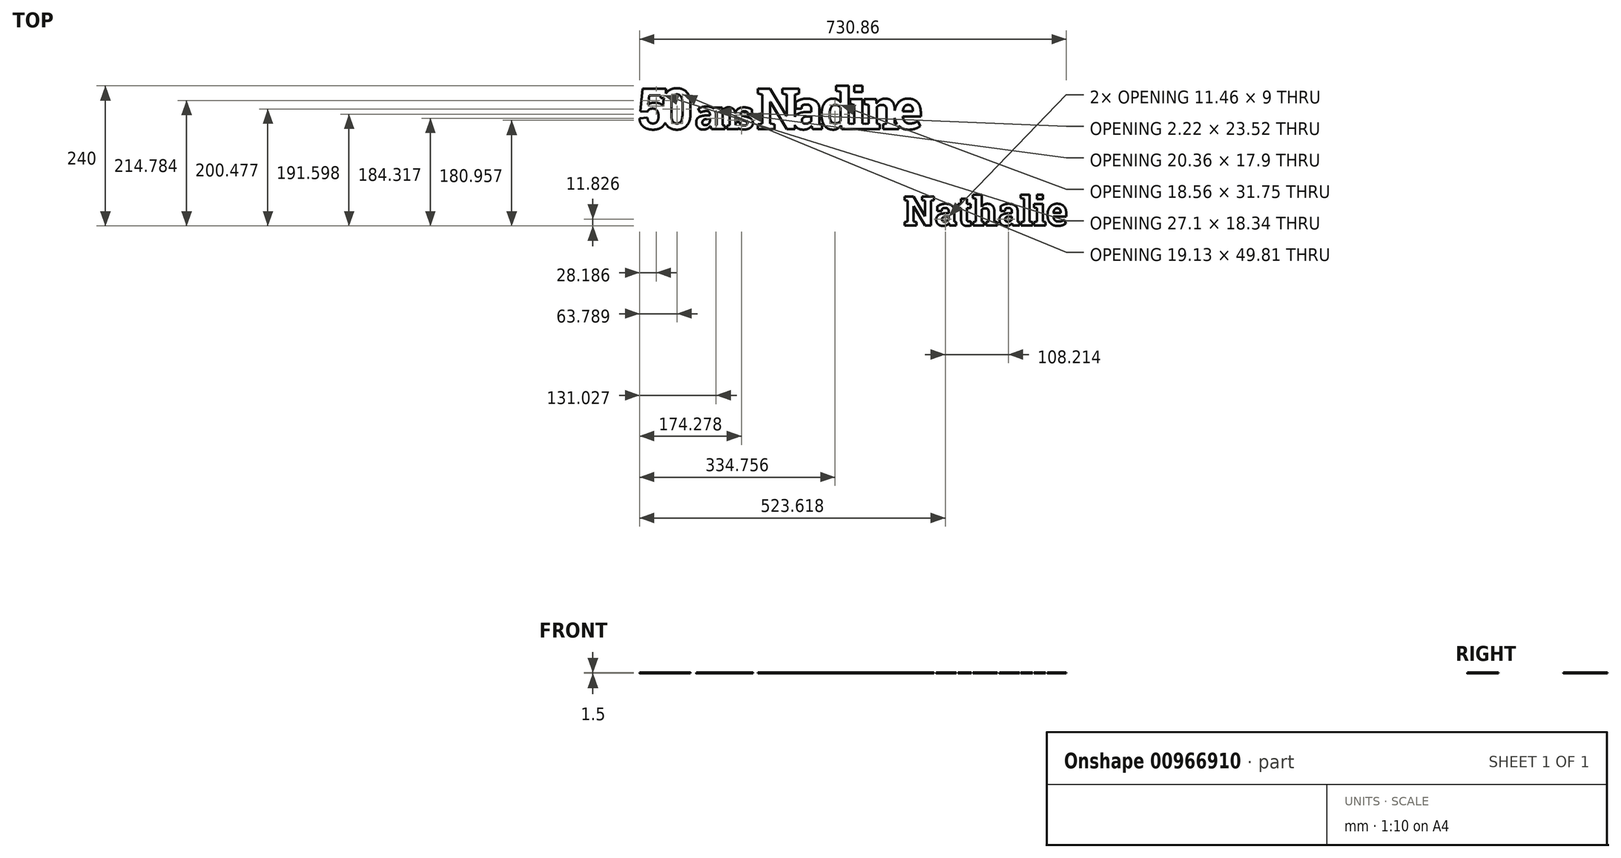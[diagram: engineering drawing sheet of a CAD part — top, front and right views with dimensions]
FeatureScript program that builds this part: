
annotation { "Feature Type Name" : "Feature", "Feature Type Description" : "" }
export const myFeature = defineFeature(function(context is Context, id is Id, definition is map)
    precondition{}
    {
        {
            var Q0;
            Q0=qCreatedBy(makeId("Top.planeOp"),FACE);
            var sketch = newSketch(context, id + "F0", { "sketchPlane" : qUnion([Q0])});
            skText(sketch, "E0", { "text": "50 ans Nathalie", "fontName": "RobotoSlab-Bold.ttf"});
            skText(sketch, "E1", { "text": "5", "fontName": "RobotoSlab-Bold.ttf"});
            skText(sketch, "E2", { "text": "0", "fontName": "RobotoSlab-Bold.ttf"});
            skLineSegment(sketch, "E3", {"start": v(-280.2, 70) * mm, "end": v(280.2, 70) * mm, "construction": true});
            skLineSegment(sketch, "E4", {"start": v(-280.2, 0) * mm, "end": v(280.2, 0) * mm, "construction": true});
            skText(sketch, "E5", { "text": "a", "fontName": "OpenSans-Bold.ttf"});
            skText(sketch, "E6", { "text": "n", "fontName": "RobotoSlab-Bold.ttf"});
            skText(sketch, "E7", { "text": "s", "fontName": "RobotoSlab-Bold.ttf"});
            skLineSegment(sketch, "E8", {"start": v(-280.2, 50) * mm, "end": v(280.2, 50) * mm, "construction": true});
            skText(sketch, "E9", { "text": "N", "fontName": "RobotoSlab-Bold.ttf"});
            skText(sketch, "E10", { "text": "a", "fontName": "RobotoSlab-Bold.ttf"});
            skLineSegment(sketch, "E11", {"start": v(280.2, 70) * mm, "end": v(280.2, 0) * mm, "construction": true});
            skText(sketch, "E12", { "text": "i", "fontName": "RobotoSlab-Bold.ttf"});
            skText(sketch, "E13", { "text": "e", "fontName": "RobotoSlab-Bold.ttf"});
            skText(sketch, "E14", { "text": "d", "fontName": "RobotoSlab-Bold.ttf"});
            skText(sketch, "E15", { "text": "n", "fontName": "RobotoSlab-Bold.ttf"});
            const initialGuessF0  = {"E0": [-0.0539, -0.16522, 1, 0, 0.05], "E1": [-0.2802, 0, 1, 0, 0.07], "E2": [-0.24123, 0, 1, 0, 0.07], "E5": [-0.18318, 0, 1, 0, 0.05], "E6": [-0.15123, 0, 1, 0, 0.05], "E7": [-0.11641, 0, 1, 0, 0.05], "E9": [-0.0772, 0, 1, 0, 0.07], "E10": [-0.0164, 0, 1, 0, 0.07], "E12": [0.08157, 0, 1, 0, 0.07], "E13": [0.15634, 0, 1, 0, 0.07], "E14": [0.0314, 0, 1, 0, 0.07], "E15": [0.1063, 0, 1, 0, 0.07]};
            skSetInitialGuess(sketch, initialGuessF0);
            skSolve(sketch);
        }
        {
            var Q0;
            {var subQ4=sQuery(id+"F0.wireOp",EDGE,"E13.sketch_text.stroke-1");var subQ9=sQuery(id+"F0.wireOp",EDGE,"E13.sketch_text.stroke-0");var subQ10=makeQuery(id+"F0.imprint","INTERSECT",VERTEX,{"derivedFrom":[subQ9,subQ4]});var subQ15=makeQuery(id+"F0.imprint","IMPRINT",EDGE,{"disambiguationData":[TD([[subQ10,1.0]])],"derivedFrom":subQ9});var subQ16=sQuery(id+"F0.wireOp",EDGE,"E12.sketch_text.stroke-7");var subQ21=sQuery(id+"F0.wireOp",EDGE,"E13.sketch_text.stroke-2");var subQ23=makeQuery(id+"F0.imprint","IMPRINT",EDGE,{"derivedFrom":subQ21});var subQ24=makeQuery(id+"F0.imprint","IMPRINT",EDGE,{"derivedFrom":subQ16});var subQ33=sQuery(id+"F0.wireOp",EDGE,"E12.sketch_text.stroke-9");var subQ34=makeQuery(id+"F0.imprint","IMPRINT",EDGE,{"derivedFrom":subQ33});var subQ43=sQuery(id+"F0.wireOp",EDGE,"E12.sketch_text.stroke-1");var subQ48=sQuery(id+"F0.wireOp",EDGE,"E13.sketch_text.stroke-4");var subQ57=sQuery(id+"F0.wireOp",EDGE,"E6.sketch_text.stroke-11");var subQ59=sQuery(id+"F0.wireOp",EDGE,"E7.sketch_text.stroke-14");var subQ60=makeQuery(id+"F0.imprint","INTERSECT",VERTEX,{"derivedFrom":[subQ57,subQ59]});var subQ61=sQuery(id+"F0.wireOp",EDGE,"E6.sketch_text.stroke-9");var subQ64=sQuery(id+"F0.wireOp",EDGE,"E7.sketch_text.stroke-25");var subQ66=makeQuery(id+"F0.imprint","INTERSECT",VERTEX,{"derivedFrom":[subQ61,subQ64]});var subQ69=sQuery(id+"F0.wireOp",EDGE,"E6.sketch_text.stroke-1");var subQ79=sQuery(id+"F0.wireOp",EDGE,"E6.sketch_text.stroke-2");var subQ80=sQuery(id+"F0.wireOp",EDGE,"E5.sketch_text.stroke-15");var subQ81=makeQuery(id+"F0.imprint","INTERSECT",VERTEX,{"derivedFrom":[subQ80,subQ79]});var subQ85=makeQuery(id+"F0.imprint","IMPRINT",EDGE,{"disambiguationData":[TD([[subQ81,1.0]])],"derivedFrom":subQ80});var subQ88=sQuery(id+"F0.wireOp",EDGE,"E5.sketch_text.stroke-0");var subQ89=sQuery(id+"F0.wireOp",EDGE,"E6.sketch_text.stroke-25");var subQ93=makeQuery(id+"F0.imprint","IMPRINT",EDGE,{"derivedFrom":subQ89});var subQ102=makeQuery(id+"F0.imprint","IMPRINT",EDGE,{"disambiguationData":[TD([[subQ66,-1.0]])],"derivedFrom":subQ61});var subQ103=makeQuery(id+"F0.imprint","IMPRINT",EDGE,{"disambiguationData":[TD([[subQ60,-1.0]])],"derivedFrom":subQ57});var subQ108=sQuery(id+"F0.wireOp",EDGE,"E1.sketch_text.stroke-24");var subQ110=sQuery(id+"F0.wireOp",EDGE,"E1.sketch_text.stroke-25");var subQ114=makeQuery(id+"F0.imprint","INTERSECT",VERTEX,{"derivedFrom":[subQ108,subQ110]});var subQ115=makeQuery(id+"F0.imprint","IMPRINT",EDGE,{"disambiguationData":[TD([[subQ114,1.0]])],"derivedFrom":subQ108});var subQ116=sQuery(id+"F0.wireOp",EDGE,"E1.sketch_text.stroke-6");var subQ117=makeQuery(id+"F0.imprint","IMPRINT",EDGE,{"derivedFrom":subQ116});var subQ127=sQuery(id+"F0.wireOp",EDGE,"E1.sketch_text.stroke-0");var subQ135=sQuery(id+"F0.wireOp",EDGE,"E10.sketch_text.stroke-6");var subQ136=sQuery(id+"F0.wireOp",EDGE,"E9.sketch_text.stroke-2");var subQ137=makeQuery(id+"F0.imprint","INTERSECT",VERTEX,{"derivedFrom":[subQ136,subQ135]});var subQ140=makeQuery(id+"F0.imprint","IMPRINT",EDGE,{"disambiguationData":[TD([[subQ137,-1.0]])],"derivedFrom":subQ136});Q0=qUnion([makeQuery(id+"F0.imprint","IMPRINT",FACE,{"disambiguationData":[TD([[makeQuery(id+"F0.imprint","IMPRINT",EDGE,{"derivedFrom":sQuery(id+"F0.wireOp",EDGE,"E0.sketch_text.stroke-0")}),-1.0]])]}),makeQuery(id+"F0.imprint","IMPRINT",FACE,{"disambiguationData":[TD([[makeQuery(id+"F0.imprint","IMPRINT",EDGE,{"derivedFrom":sQuery(id+"F0.wireOp",EDGE,"E0.sketch_text.stroke-81")}),-1.0]])]}),makeQuery(id+"F0.imprint","IMPRINT",FACE,{"disambiguationData":[TD([[makeQuery(id+"F0.imprint","IMPRINT",EDGE,{"derivedFrom":sQuery(id+"F0.wireOp",EDGE,"E0.sketch_text.stroke-107")}),-1.0]])]}),makeQuery(id+"F0.imprint","IMPRINT",FACE,{"disambiguationData":[TD([[makeQuery(id+"F0.imprint","IMPRINT",EDGE,{"derivedFrom":sQuery(id+"F0.wireOp",EDGE,"E0.sketch_text.stroke-137")}),-1.0]])]}),makeQuery(id+"F0.imprint","IMPRINT",FACE,{"disambiguationData":[TD([[makeQuery(id+"F0.imprint","IMPRINT",EDGE,{"derivedFrom":sQuery(id+"F0.wireOp",EDGE,"E0.sketch_text.stroke-196")}),-1.0]])]}),makeQuery(id+"F0.imprint","IMPRINT",FACE,{"disambiguationData":[TD([[makeQuery(id+"F0.imprint","IMPRINT",EDGE,{"derivedFrom":sQuery(id+"F0.wireOp",EDGE,"E0.sketch_text.stroke-216")}),-1.0]])]}),makeQuery(id+"F0.imprint","IMPRINT",FACE,{"disambiguationData":[TD([[makeQuery(id+"F0.imprint","IMPRINT",EDGE,{"derivedFrom":sQuery(id+"F0.wireOp",EDGE,"E0.sketch_text.stroke-277")}),-1.0]])]}),makeQuery(id+"F0.imprint","IMPRINT",FACE,{"disambiguationData":[TD([[makeQuery(id+"F0.imprint","IMPRINT",EDGE,{"derivedFrom":sQuery(id+"F0.wireOp",EDGE,"E0.sketch_text.stroke-287")}),-1.0]])]}),makeQuery(id+"F0.imprint","IMPRINT",FACE,{"disambiguationData":[TD([[makeQuery(id+"F0.imprint","IMPRINT",EDGE,{"derivedFrom":sQuery(id+"F0.wireOp",EDGE,"E0.sketch_text.stroke-297")}),-1.0]])]}),makeQuery(id+"F0.imprint","IMPRINT",FACE,{"disambiguationData":[TD([[makeQuery(id+"F0.imprint","IMPRINT",EDGE,{"derivedFrom":sQuery(id+"F0.wireOp",EDGE,"E12.sketch_text.stroke-10")}),-1.0]])]}),makeQuery(id+"F0.imprint","IMPRINT",FACE,{"disambiguationData":[TD([[makeQuery(id+"F0.imprint","IMPRINT",EDGE,{"derivedFrom":sQuery(id+"F0.wireOp",EDGE,"E0.sketch_text.stroke-26")}),-1.0]])]}),makeQuery(id+"F0.imprint","IMPRINT",FACE,{"disambiguationData":[TD([[makeQuery(id+"F0.imprint","IMPRINT",EDGE,{"derivedFrom":sQuery(id+"F0.wireOp",EDGE,"E0.sketch_text.stroke-46")}),-1.0]])]}),makeQuery(id+"F0.imprint","IMPRINT",FACE,{"disambiguationData":[TD([[makeQuery(id+"F0.imprint","IMPRINT",EDGE,{"derivedFrom":sQuery(id+"F0.wireOp",EDGE,"E0.sketch_text.stroke-161")}),-1.0]])]}),makeQuery(id+"F0.imprint","IMPRINT",FACE,{"disambiguationData":[TD([[makeQuery(id+"F0.imprint","IMPRINT",EDGE,{"derivedFrom":sQuery(id+"F0.wireOp",EDGE,"E0.sketch_text.stroke-242")}),-1.0]])]}),makeQuery(id+"F0.imprint","IMPRINT",FACE,{"disambiguationData":[TD([[makeQuery(id+"F0.imprint","IMPRINT",EDGE,{"derivedFrom":sQuery(id+"F0.wireOp",EDGE,"E0.sketch_text.stroke-301")}),-1.0]])]}),makeQuery(id+"F0.imprint","IMPRINT",FACE,{"disambiguationData":[TD([[makeQuery(id+"F0.imprint","IMPRINT",EDGE,{"derivedFrom":sQuery(id+"F0.wireOp",EDGE,"E9.sketch_text.stroke-0")}),-1.0]])]}),makeQuery(id+"F0.imprint","IMPRINT",FACE,{"disambiguationData":[TD([[makeQuery(id+"F0.imprint","IMPRINT",EDGE,{"derivedFrom":sQuery(id+"F0.wireOp",EDGE,"E10.sketch_text.stroke-0")}),-1.0]])]}),makeQuery(id+"F0.imprint","IMPRINT",FACE,{"disambiguationData":[TD([[subQ140,-1.0]])]}),makeQuery(id+"F0.imprint","IMPRINT",FACE,{"disambiguationData":[TD([[subQ117,-1.0]])]}),makeQuery(id+"F0.imprint","IMPRINT",FACE,{"disambiguationData":[TD([[subQ115,-1.0]])]}),makeQuery(id+"F0.imprint","IMPRINT",FACE,{"disambiguationData":[TD([[makeQuery(id+"F0.imprint","IMPRINT",EDGE,{"derivedFrom":subQ127}),-1.0]])]}),makeQuery(id+"F0.imprint","IMPRINT",FACE,{"disambiguationData":[TD([[subQ117,1.0]])]}),makeQuery(id+"F0.imprint","IMPRINT",FACE,{"disambiguationData":[TD([[subQ85,-1.0]])]}),makeQuery(id+"F0.imprint","IMPRINT",FACE,{"disambiguationData":[TD([[subQ93,-1.0]])]}),makeQuery(id+"F0.imprint","IMPRINT",FACE,{"disambiguationData":[TD([[subQ102,-1.0]])]}),makeQuery(id+"F0.imprint","IMPRINT",FACE,{"disambiguationData":[TD([[subQ103,-1.0]])]}),makeQuery(id+"F0.imprint","IMPRINT",FACE,{"disambiguationData":[TD([[makeQuery(id+"F0.imprint","IMPRINT",EDGE,{"derivedFrom":sQuery(id+"F0.wireOp",EDGE,"E7.sketch_text.stroke-0")}),-1.0]])]}),makeQuery(id+"F0.imprint","IMPRINT",FACE,{"disambiguationData":[TD([[makeQuery(id+"F0.imprint","IMPRINT",EDGE,{"derivedFrom":subQ88}),-1.0]])]}),makeQuery(id+"F0.imprint","IMPRINT",FACE,{"disambiguationData":[TD([[makeQuery(id+"F0.imprint","IMPRINT",EDGE,{"derivedFrom":subQ69}),-1.0]])]}),makeQuery(id+"F0.imprint","IMPRINT",FACE,{"disambiguationData":[TD([[subQ15,-1.0]])]}),makeQuery(id+"F0.imprint","IMPRINT",FACE,{"disambiguationData":[TD([[subQ24,-1.0]])]}),makeQuery(id+"F0.imprint","IMPRINT",FACE,{"disambiguationData":[TD([[subQ34,1.0]])]}),makeQuery(id+"F0.imprint","IMPRINT",FACE,{"disambiguationData":[TD([[subQ23,-1.0]])]}),makeQuery(id+"F0.imprint","IMPRINT",FACE,{"disambiguationData":[TD([[makeQuery(id+"F0.imprint","IMPRINT",EDGE,{"derivedFrom":subQ48}),-1.0]])]}),makeQuery(id+"F0.imprint","IMPRINT",FACE,{"disambiguationData":[TD([[makeQuery(id+"F0.imprint","IMPRINT",EDGE,{"derivedFrom":subQ43}),-1.0]])]}),makeQuery(id+"F0.imprint","IMPRINT",FACE,{"disambiguationData":[TD([[subQ34,-1.0]])]}),makeQuery(id+"F0.imprint","IMPRINT",FACE,{"disambiguationData":[TD([[subQ24,1.0]])]})]);}
            extrude(context, id + "F1", {"entities" : qUnion([Q0]), "depth" : 1.5 * mm, "offsetDistance" : 25 * mm});
        }
        {
            var Q0;
            Q0=makeQuery(id+"F1.opExtrude","SWEPT_BODY",BODY,{"disambiguationData":[OSD([sQuery(id+"F0.wireOp",EDGE,"E0.sketch_text.stroke-0"),sQuery(id+"F0.wireOp",EDGE,"E0.sketch_text.stroke-1"),sQuery(id+"F0.wireOp",EDGE,"E0.sketch_text.stroke-2"),sQuery(id+"F0.wireOp",EDGE,"E0.sketch_text.stroke-3"),sQuery(id+"F0.wireOp",EDGE,"E0.sketch_text.stroke-4"),sQuery(id+"F0.wireOp",EDGE,"E0.sketch_text.stroke-5"),sQuery(id+"F0.wireOp",EDGE,"E0.sketch_text.stroke-6"),sQuery(id+"F0.wireOp",EDGE,"E0.sketch_text.stroke-7"),sQuery(id+"F0.wireOp",EDGE,"E0.sketch_text.stroke-8"),sQuery(id+"F0.wireOp",EDGE,"E0.sketch_text.stroke-9"),sQuery(id+"F0.wireOp",EDGE,"E0.sketch_text.stroke-10"),sQuery(id+"F0.wireOp",EDGE,"E0.sketch_text.stroke-11"),sQuery(id+"F0.wireOp",EDGE,"E0.sketch_text.stroke-12"),sQuery(id+"F0.wireOp",EDGE,"E0.sketch_text.stroke-13"),sQuery(id+"F0.wireOp",EDGE,"E0.sketch_text.stroke-14"),sQuery(id+"F0.wireOp",EDGE,"E0.sketch_text.stroke-15"),sQuery(id+"F0.wireOp",EDGE,"E0.sketch_text.stroke-16"),sQuery(id+"F0.wireOp",EDGE,"E0.sketch_text.stroke-17"),sQuery(id+"F0.wireOp",EDGE,"E0.sketch_text.stroke-18"),sQuery(id+"F0.wireOp",EDGE,"E0.sketch_text.stroke-19"),sQuery(id+"F0.wireOp",EDGE,"E0.sketch_text.stroke-20"),sQuery(id+"F0.wireOp",EDGE,"E0.sketch_text.stroke-21"),sQuery(id+"F0.wireOp",EDGE,"E0.sketch_text.stroke-22"),sQuery(id+"F0.wireOp",EDGE,"E0.sketch_text.stroke-23"),sQuery(id+"F0.wireOp",EDGE,"E0.sketch_text.stroke-24"),sQuery(id+"F0.wireOp",EDGE,"E0.sketch_text.stroke-25")])]});
            var Q1;
            Q1=makeQuery(id+"F1.opExtrude","SWEPT_BODY",BODY,{"disambiguationData":[OSD([sQuery(id+"F0.wireOp",EDGE,"E0.sketch_text.stroke-26"),sQuery(id+"F0.wireOp",EDGE,"E0.sketch_text.stroke-27"),sQuery(id+"F0.wireOp",EDGE,"E0.sketch_text.stroke-28"),sQuery(id+"F0.wireOp",EDGE,"E0.sketch_text.stroke-29"),sQuery(id+"F0.wireOp",EDGE,"E0.sketch_text.stroke-30"),sQuery(id+"F0.wireOp",EDGE,"E0.sketch_text.stroke-31"),sQuery(id+"F0.wireOp",EDGE,"E0.sketch_text.stroke-32"),sQuery(id+"F0.wireOp",EDGE,"E0.sketch_text.stroke-33"),sQuery(id+"F0.wireOp",EDGE,"E0.sketch_text.stroke-34"),sQuery(id+"F0.wireOp",EDGE,"E0.sketch_text.stroke-35"),sQuery(id+"F0.wireOp",EDGE,"E0.sketch_text.stroke-36"),sQuery(id+"F0.wireOp",EDGE,"E0.sketch_text.stroke-37"),sQuery(id+"F0.wireOp",EDGE,"E0.sketch_text.stroke-38"),sQuery(id+"F0.wireOp",EDGE,"E0.sketch_text.stroke-39"),sQuery(id+"F0.wireOp",EDGE,"E0.sketch_text.stroke-40"),sQuery(id+"F0.wireOp",EDGE,"E0.sketch_text.stroke-41"),sQuery(id+"F0.wireOp",EDGE,"E0.sketch_text.stroke-42"),sQuery(id+"F0.wireOp",EDGE,"E0.sketch_text.stroke-43"),sQuery(id+"F0.wireOp",EDGE,"E0.sketch_text.stroke-44"),sQuery(id+"F0.wireOp",EDGE,"E0.sketch_text.stroke-45")])]});
            var Q2;
            Q2=makeQuery(id+"F1.opExtrude","SWEPT_BODY",BODY,{"disambiguationData":[OSD([sQuery(id+"F0.wireOp",EDGE,"E0.sketch_text.stroke-46"),sQuery(id+"F0.wireOp",EDGE,"E0.sketch_text.stroke-47"),sQuery(id+"F0.wireOp",EDGE,"E0.sketch_text.stroke-48"),sQuery(id+"F0.wireOp",EDGE,"E0.sketch_text.stroke-49"),sQuery(id+"F0.wireOp",EDGE,"E0.sketch_text.stroke-50"),sQuery(id+"F0.wireOp",EDGE,"E0.sketch_text.stroke-51"),sQuery(id+"F0.wireOp",EDGE,"E0.sketch_text.stroke-52"),sQuery(id+"F0.wireOp",EDGE,"E0.sketch_text.stroke-53"),sQuery(id+"F0.wireOp",EDGE,"E0.sketch_text.stroke-54"),sQuery(id+"F0.wireOp",EDGE,"E0.sketch_text.stroke-55"),sQuery(id+"F0.wireOp",EDGE,"E0.sketch_text.stroke-56"),sQuery(id+"F0.wireOp",EDGE,"E0.sketch_text.stroke-57"),sQuery(id+"F0.wireOp",EDGE,"E0.sketch_text.stroke-58"),sQuery(id+"F0.wireOp",EDGE,"E0.sketch_text.stroke-59"),sQuery(id+"F0.wireOp",EDGE,"E0.sketch_text.stroke-60"),sQuery(id+"F0.wireOp",EDGE,"E0.sketch_text.stroke-61"),sQuery(id+"F0.wireOp",EDGE,"E0.sketch_text.stroke-62"),sQuery(id+"F0.wireOp",EDGE,"E0.sketch_text.stroke-63"),sQuery(id+"F0.wireOp",EDGE,"E0.sketch_text.stroke-64"),sQuery(id+"F0.wireOp",EDGE,"E0.sketch_text.stroke-65"),sQuery(id+"F0.wireOp",EDGE,"E0.sketch_text.stroke-66"),sQuery(id+"F0.wireOp",EDGE,"E0.sketch_text.stroke-67"),sQuery(id+"F0.wireOp",EDGE,"E0.sketch_text.stroke-68"),sQuery(id+"F0.wireOp",EDGE,"E0.sketch_text.stroke-69"),sQuery(id+"F0.wireOp",EDGE,"E0.sketch_text.stroke-70"),sQuery(id+"F0.wireOp",EDGE,"E0.sketch_text.stroke-71"),sQuery(id+"F0.wireOp",EDGE,"E0.sketch_text.stroke-72"),sQuery(id+"F0.wireOp",EDGE,"E0.sketch_text.stroke-73"),sQuery(id+"F0.wireOp",EDGE,"E0.sketch_text.stroke-74"),sQuery(id+"F0.wireOp",EDGE,"E0.sketch_text.stroke-75"),sQuery(id+"F0.wireOp",EDGE,"E0.sketch_text.stroke-76"),sQuery(id+"F0.wireOp",EDGE,"E0.sketch_text.stroke-77"),sQuery(id+"F0.wireOp",EDGE,"E0.sketch_text.stroke-78"),sQuery(id+"F0.wireOp",EDGE,"E0.sketch_text.stroke-79"),sQuery(id+"F0.wireOp",EDGE,"E0.sketch_text.stroke-80")])]});
            var Q3;
            Q3=makeQuery(id+"F1.opExtrude","SWEPT_BODY",BODY,{"disambiguationData":[OSD([sQuery(id+"F0.wireOp",EDGE,"E0.sketch_text.stroke-107"),sQuery(id+"F0.wireOp",EDGE,"E0.sketch_text.stroke-108"),sQuery(id+"F0.wireOp",EDGE,"E0.sketch_text.stroke-109"),sQuery(id+"F0.wireOp",EDGE,"E0.sketch_text.stroke-110"),sQuery(id+"F0.wireOp",EDGE,"E0.sketch_text.stroke-111"),sQuery(id+"F0.wireOp",EDGE,"E0.sketch_text.stroke-112"),sQuery(id+"F0.wireOp",EDGE,"E0.sketch_text.stroke-113"),sQuery(id+"F0.wireOp",EDGE,"E0.sketch_text.stroke-114"),sQuery(id+"F0.wireOp",EDGE,"E0.sketch_text.stroke-115"),sQuery(id+"F0.wireOp",EDGE,"E0.sketch_text.stroke-116"),sQuery(id+"F0.wireOp",EDGE,"E0.sketch_text.stroke-117"),sQuery(id+"F0.wireOp",EDGE,"E0.sketch_text.stroke-118"),sQuery(id+"F0.wireOp",EDGE,"E0.sketch_text.stroke-119"),sQuery(id+"F0.wireOp",EDGE,"E0.sketch_text.stroke-120"),sQuery(id+"F0.wireOp",EDGE,"E0.sketch_text.stroke-121"),sQuery(id+"F0.wireOp",EDGE,"E0.sketch_text.stroke-122"),sQuery(id+"F0.wireOp",EDGE,"E0.sketch_text.stroke-123"),sQuery(id+"F0.wireOp",EDGE,"E0.sketch_text.stroke-124"),sQuery(id+"F0.wireOp",EDGE,"E0.sketch_text.stroke-125"),sQuery(id+"F0.wireOp",EDGE,"E0.sketch_text.stroke-126"),sQuery(id+"F0.wireOp",EDGE,"E0.sketch_text.stroke-127"),sQuery(id+"F0.wireOp",EDGE,"E0.sketch_text.stroke-128"),sQuery(id+"F0.wireOp",EDGE,"E0.sketch_text.stroke-129"),sQuery(id+"F0.wireOp",EDGE,"E0.sketch_text.stroke-130"),sQuery(id+"F0.wireOp",EDGE,"E0.sketch_text.stroke-131"),sQuery(id+"F0.wireOp",EDGE,"E0.sketch_text.stroke-132"),sQuery(id+"F0.wireOp",EDGE,"E0.sketch_text.stroke-133"),sQuery(id+"F0.wireOp",EDGE,"E0.sketch_text.stroke-134"),sQuery(id+"F0.wireOp",EDGE,"E0.sketch_text.stroke-135"),sQuery(id+"F0.wireOp",EDGE,"E0.sketch_text.stroke-136")])]});
            var Q4;
            Q4=makeQuery(id+"F1.opExtrude","SWEPT_BODY",BODY,{"disambiguationData":[OSD([sQuery(id+"F0.wireOp",EDGE,"E0.sketch_text.stroke-81"),sQuery(id+"F0.wireOp",EDGE,"E0.sketch_text.stroke-82"),sQuery(id+"F0.wireOp",EDGE,"E0.sketch_text.stroke-83"),sQuery(id+"F0.wireOp",EDGE,"E0.sketch_text.stroke-84"),sQuery(id+"F0.wireOp",EDGE,"E0.sketch_text.stroke-85"),sQuery(id+"F0.wireOp",EDGE,"E0.sketch_text.stroke-86"),sQuery(id+"F0.wireOp",EDGE,"E0.sketch_text.stroke-87"),sQuery(id+"F0.wireOp",EDGE,"E0.sketch_text.stroke-88"),sQuery(id+"F0.wireOp",EDGE,"E0.sketch_text.stroke-89"),sQuery(id+"F0.wireOp",EDGE,"E0.sketch_text.stroke-90"),sQuery(id+"F0.wireOp",EDGE,"E0.sketch_text.stroke-91"),sQuery(id+"F0.wireOp",EDGE,"E0.sketch_text.stroke-92"),sQuery(id+"F0.wireOp",EDGE,"E0.sketch_text.stroke-93"),sQuery(id+"F0.wireOp",EDGE,"E0.sketch_text.stroke-94"),sQuery(id+"F0.wireOp",EDGE,"E0.sketch_text.stroke-95"),sQuery(id+"F0.wireOp",EDGE,"E0.sketch_text.stroke-96"),sQuery(id+"F0.wireOp",EDGE,"E0.sketch_text.stroke-97"),sQuery(id+"F0.wireOp",EDGE,"E0.sketch_text.stroke-98"),sQuery(id+"F0.wireOp",EDGE,"E0.sketch_text.stroke-99"),sQuery(id+"F0.wireOp",EDGE,"E0.sketch_text.stroke-100"),sQuery(id+"F0.wireOp",EDGE,"E0.sketch_text.stroke-101"),sQuery(id+"F0.wireOp",EDGE,"E0.sketch_text.stroke-102"),sQuery(id+"F0.wireOp",EDGE,"E0.sketch_text.stroke-103"),sQuery(id+"F0.wireOp",EDGE,"E0.sketch_text.stroke-104"),sQuery(id+"F0.wireOp",EDGE,"E0.sketch_text.stroke-105"),sQuery(id+"F0.wireOp",EDGE,"E0.sketch_text.stroke-106")])]});
            deleteBodies(context, id + "F2", {"entities" : qUnion([Q0, Q1, Q2, Q3, Q4])});
        }
    });
